# Revit family: Sanitary_Accessories_Johnson-Suisse_Cube_Wall_Tumbler_Holder
name_source: partatom
category: Plumbing Fixtures
revit_build: Autodesk Revit 2015 (Build: 20140606_1530(x64)
units: mm (PartAtom-declared; Revit-internal decimal feet)

## types (1)
- Cube Wall Tumbler Holder
    BIMobject category = Accessories
    Brand url = http://www.johnsonsuisse.com.au
    Design country = Spain
    EAN code = https://9325304004501
    Edition number = 1
    IFC Classification = Furnishing Element
    Manufacturer country = China
    Manufacturer name = Johnson Suisse
    Material main = Metal
    Material secondary = Chrome
    NBS Reference Code = 35-75-92
    NBS Reference Description = Tumbler Holders
    Nominal height = 120 mm  [stored 0.393701 ft]
    Nominal width = 75 mm  [stored 0.246063 ft]
    Product Guid = 31e7d8ab-c66a-41e6-ab9b-8d391fcd58b0
    Product SKU = GDC160152
    Product data url = https://bimobject.com
    Product family = Cube
    Product group = Accessories
    Product url = https://johnsonsuisse.com.au
    QR code = http://bimobject.com
    Technical description = https://johnsonsuisse.com.au
    Type = cube_wall_tumbler_holder : Default
    UNSPSC Code = 301815
    Uniclass 1.4 Code = L824
    Uniclass 1.4 Description = Bathroom, toilet furniture and fittings
    Uniclass 2.0 Code = PR-35-75-92
    Uniclass 2.0 Description = Tumbler Holders
    Uniclass 2015 Code = Pr_40_20_76_92
    Uniclass 2015 Name = Tumbler holders
    Weight Net (Kg) = 0.464

note: [stored X ft] marks values corroborated as IEEE doubles in the binary element streams (Revit-internal decimal feet)

## geometry (parser evidence)
native form markers: Sweep x5
no freeform markers — native parametric forms only
